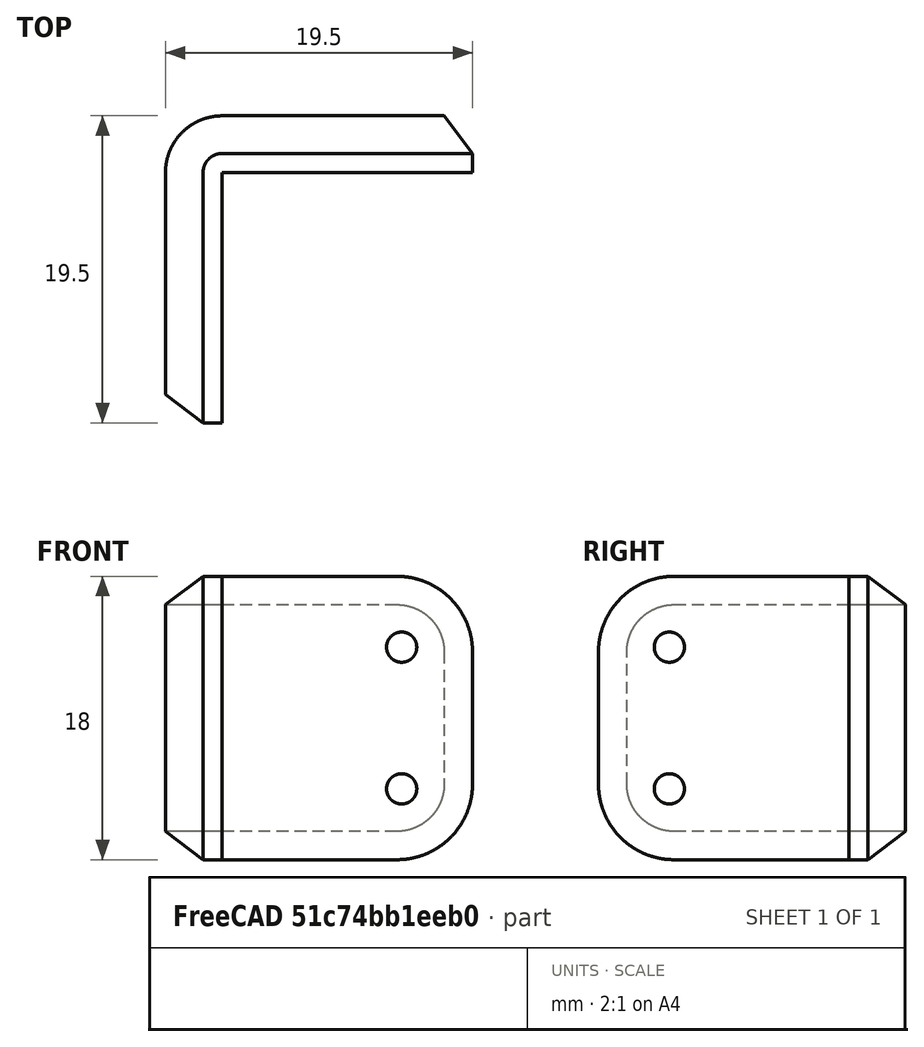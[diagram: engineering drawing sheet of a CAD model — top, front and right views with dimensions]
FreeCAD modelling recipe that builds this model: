
FCSTD DOCUMENT  (FreeCAD 0.19R24267 +148 (Git))
Label: Top Angle - Small
License: All rights reserved
LicenseURL: http://en.wikipedia.org/wiki/All_rights_reserved
objects: Part::FeaturePython×1, PartDesign::FeatureBase×1, PartDesign::Body×1, App::MeasureDistance×1
note: 3 computed .brp shape members not serialized (recipe doc carries the construction recipe); baked Part::Feature solids carry a one-line shape summary decoded from their .brp

FEATURE [Part::FeaturePython] Clone  label="Top_angle001 (Solid)001"  # WARN: FeaturePython — macro-defined, semantics opaque (R4)
  AttacherType = Attacher::AttachEngine3D
  Fuse = false
  Scale = (0.6,0.6,0.6)
FEATURE [PartDesign::FeatureBase] BaseFeature
  BaseFeature = -> Clone
FEATURE [PartDesign::Body] Body
  BaseFeature = -> Clone
  Group = -> [BaseFeature]
  Origin = -> Origin
  Tip = -> BaseFeature
FEATURE [App::MeasureDistance] Distance  label="Distance: 1.92 mm"
  Distance = 1.91954
  P1 = (14.04,19.5,4.49162)
  P2 = (15.9594,19.5,4.4665)
